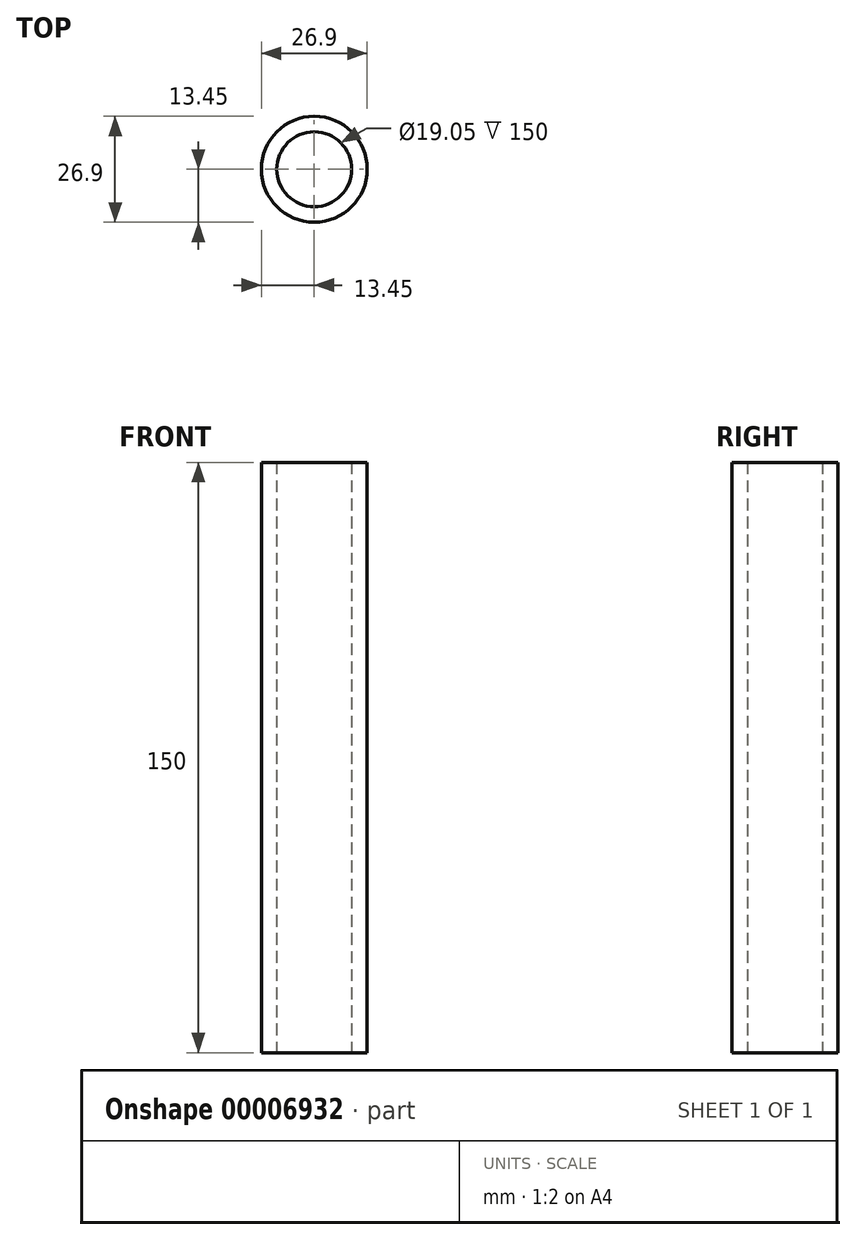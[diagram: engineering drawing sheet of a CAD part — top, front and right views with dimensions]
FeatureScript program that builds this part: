
annotation { "Feature Type Name" : "Feature", "Feature Type Description" : "" }
export const myFeature = defineFeature(function(context is Context, id is Id, definition is map)
    precondition{}
    {
        {
            var Q0;
            Q0=qCreatedBy(makeId("Top.planeOp"),FACE);
            var sketch = newSketch(context, id + "F0", { "sketchPlane" : qUnion([Q0])});
            skCircle(sketch, "E0", {"center": v(0, 0) * mm, "radius": 13.45 * mm});
            skCircle(sketch, "E1", {"center": v(0, 0) * mm, "radius": 9.53 * mm});
            skSolve(sketch);
        }
        {
            var Q0;
            Q0=makeQuery(id+"F0.imprint","IMPRINT",FACE,{"disambiguationData":[TD([[makeQuery(id+"F0.imprint","IMPRINT",EDGE,{"derivedFrom":sQuery(id+"F0.wireOp",EDGE,"E0")}),1.0]])]});
            extrude(context, id + "F1", {"entities" : qUnion([Q0]), "depth" : 150 * mm});
        }
    });
